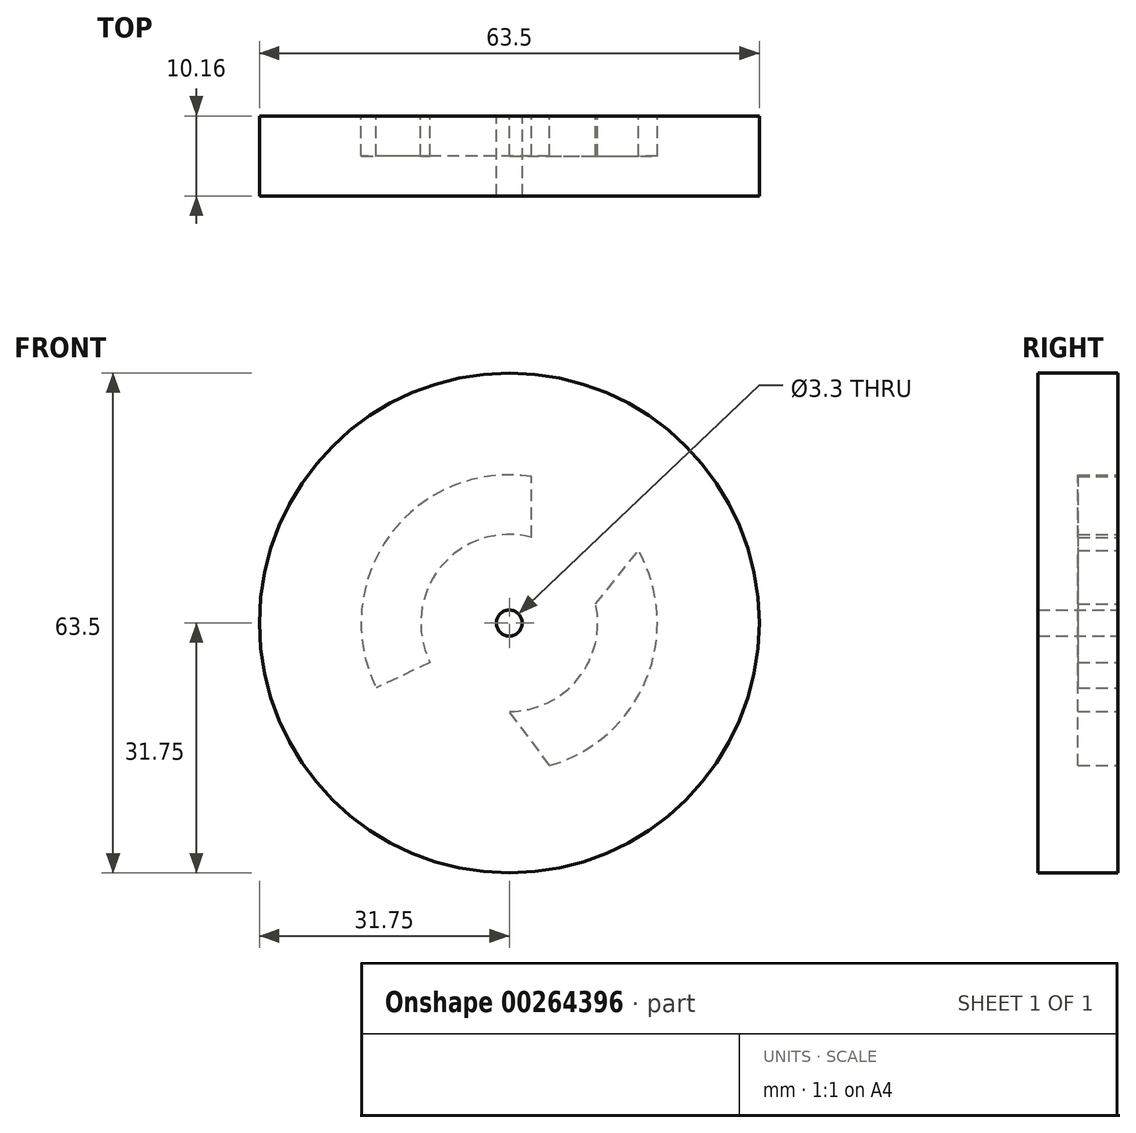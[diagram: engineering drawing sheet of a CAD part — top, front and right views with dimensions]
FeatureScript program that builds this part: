
annotation { "Feature Type Name" : "Feature", "Feature Type Description" : "" }
export const myFeature = defineFeature(function(context is Context, id is Id, definition is map)
    precondition{}
    {
        {
            var Q0;
            Q0=qCreatedBy(makeId("Front.planeOp"),FACE);
            var sketch = newSketch(context, id + "F0", { "sketchPlane" : qUnion([Q0])});
            skCircle(sketch, "E0", {"center": v(0, 0) * mm, "radius": 31.75 * mm});
            skCircle(sketch, "E1", {"center": v(0, 0) * mm, "radius": 1.65 * mm});
            skSolve(sketch);
        }
        {
            var Q0;
            Q0=qSketchRegion(id+"F0",true);
            extrude(context, id + "F1", {"entities" : qUnion([Q0]), "depth" : 10.16 * mm});
        }
        {
            var Q0;
            Q0=qCreatedBy(makeId("Front.planeOp"),FACE);
            var sketch = newSketch(context, id + "F2", { "sketchPlane" : qUnion([Q0])});
            skArc(sketch, "E2", {"start": v(2.85, 18.6) * mm, "mid": v(-15.16, 11.15) * mm, "end": v(-16.91, -8.25) * mm});
            skArc(sketch, "E3", {"start": v(2.85, 10.87) * mm, "mid": v(-8.72, 7.09) * mm, "end": v(-10.06, -5) * mm});
            skLineSegment(sketch, "E4", {"start": v(2.85, 10.87) * mm, "end": v(2.85, 18.6) * mm});
            skLineSegment(sketch, "E5", {"start": v(10.98, 2.4) * mm, "end": v(16.4, 9.22) * mm});
            skLineSegment(sketch, "E6", {"start": v(-10.06, -5) * mm, "end": v(-16.91, -8.25) * mm});
            skArc(sketch, "E7.trimOffspring", {"start": v(5.14, -18.1) * mm, "mid": v(17.4, -7.17) * mm, "end": v(16.4, 9.22) * mm});
            skLineSegment(sketch, "E8", {"start": v(5.14, -18.1) * mm, "end": v(0, -11.24) * mm});
            skArc(sketch, "E9.trimOffspring", {"start": v(0, -11.24) * mm, "mid": v(8.76, -7.05) * mm, "end": v(10.98, 2.4) * mm});
            skSolve(sketch);
        }
        {
            var Q0;
            Q0 = qSketchRegion(id + "F2", true);
            extrude(context, id + "F3", {"entities" : qUnion([Q0]), "operationType" : NewBodyOperationType.REMOVE, "oppositeDirection" : true, "depth" : -5.08 * mm});
        }
    });
